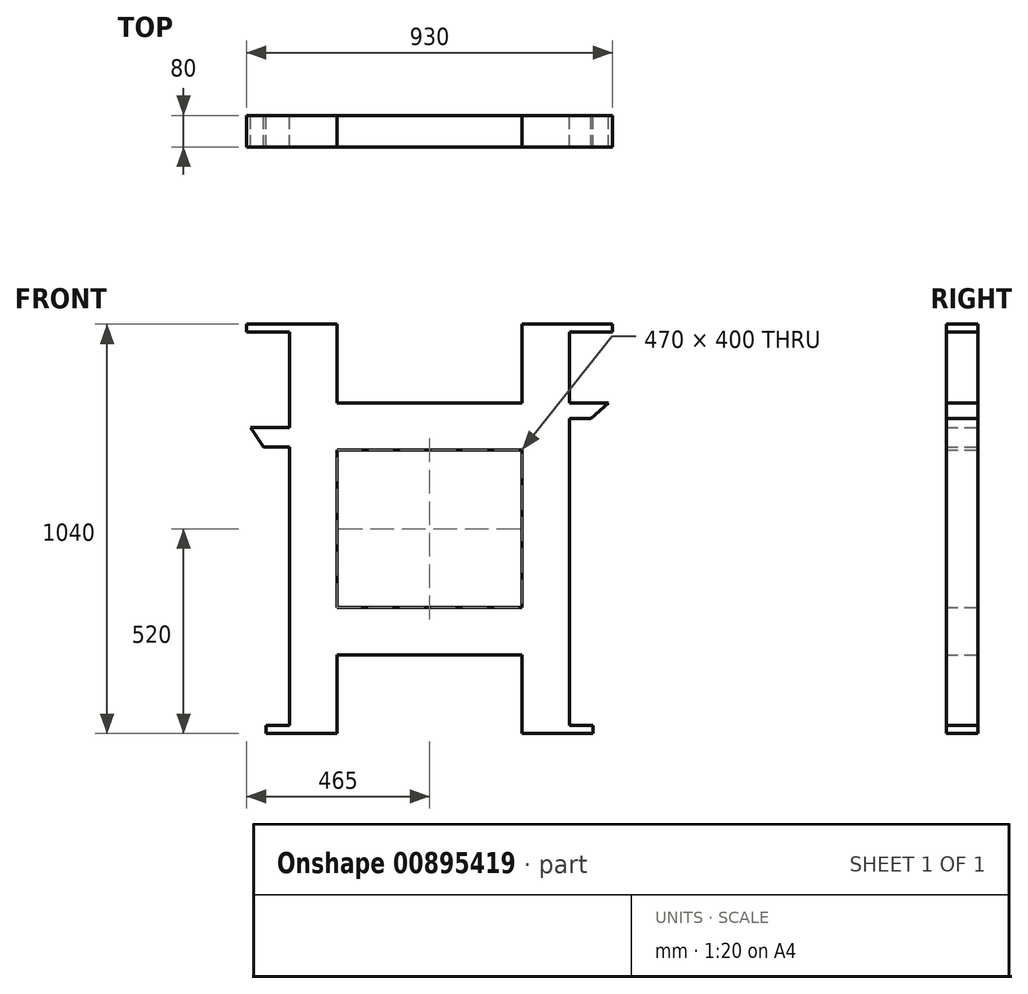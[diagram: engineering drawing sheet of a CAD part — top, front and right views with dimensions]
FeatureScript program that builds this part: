
annotation { "Feature Type Name" : "Feature", "Feature Type Description" : "" }
export const myFeature = defineFeature(function(context is Context, id is Id, definition is map)
    precondition{}
    {
        {
            var Q0;
            Q0=qCreatedBy(makeId("Front.planeOp"),FACE);
            var sketch = newSketch(context, id + "F0", { "sketchPlane" : qUnion([Q0])});
            skLineSegment(sketch, "E0.bottom", {"start": v(-355, 0) * mm, "end": v(-235, 0) * mm});
            skLineSegment(sketch, "E0.top", {"start": v(-355, -1040) * mm, "end": v(-235, -1040) * mm});
            skLineSegment(sketch, "E0.left", {"start": v(-355, -20) * mm, "end": v(-355, -262.18) * mm});
            skLineSegment(sketch, "E0.right", {"start": v(355, -20) * mm, "end": v(355, -200) * mm});
            skLineSegment(sketch, "E1.top", {"start": v(-235, -840) * mm, "end": v(235, -840) * mm});
            skLineSegment(sketch, "E1.left", {"start": v(-235, -1040) * mm, "end": v(-235, -840) * mm});
            skLineSegment(sketch, "E1.right", {"start": v(235, -1040) * mm, "end": v(235, -840) * mm});
            skLineSegment(sketch, "E2.bottom", {"start": v(-235, -720) * mm, "end": v(235, -720) * mm});
            skLineSegment(sketch, "E2.top", {"start": v(-235, -320) * mm, "end": v(235, -320) * mm});
            skLineSegment(sketch, "E2.left", {"start": v(-235, -720) * mm, "end": v(-235, -320) * mm});
            skLineSegment(sketch, "E2.right", {"start": v(235, -720) * mm, "end": v(235, -320) * mm});
            skLineSegment(sketch, "E3.bottom", {"start": v(-235, -200) * mm, "end": v(235, -200) * mm});
            skLineSegment(sketch, "E3.left", {"start": v(-235, -200) * mm, "end": v(-235, 0) * mm});
            skLineSegment(sketch, "E3.right", {"start": v(235, -200) * mm, "end": v(235, 0) * mm});
            skLineSegment(sketch, "E4.bottom", {"start": v(-355, 0) * mm, "end": v(-465, 0) * mm});
            skLineSegment(sketch, "E4.top", {"start": v(-355, -20) * mm, "end": v(-465, -20) * mm});
            skLineSegment(sketch, "E4.right", {"start": v(-465, 0) * mm, "end": v(-465, -20) * mm});
            skLineSegment(sketch, "E5.bottom", {"start": v(355, 0) * mm, "end": v(465, 0) * mm});
            skLineSegment(sketch, "E5.top", {"start": v(355, -20) * mm, "end": v(465, -20) * mm});
            skLineSegment(sketch, "E5.right", {"start": v(465, 0) * mm, "end": v(465, -20) * mm});
            skLineSegment(sketch, "E6.bottom", {"start": v(355, -1040) * mm, "end": v(415, -1040) * mm});
            skLineSegment(sketch, "E6.top", {"start": v(355, -1020) * mm, "end": v(415, -1020) * mm});
            skLineSegment(sketch, "E6.left", {"start": v(355, -1040) * mm, "end": v(355, -1020) * mm});
            skLineSegment(sketch, "E6.right", {"start": v(415, -1040) * mm, "end": v(415, -1020) * mm});
            skLineSegment(sketch, "E7.bottom", {"start": v(-355, -1040) * mm, "end": v(-415, -1040) * mm});
            skLineSegment(sketch, "E7.top", {"start": v(-355, -1020) * mm, "end": v(-415, -1020) * mm});
            skLineSegment(sketch, "E7.left", {"start": v(-355, -1040) * mm, "end": v(-355, -1020) * mm});
            skLineSegment(sketch, "E7.right", {"start": v(-415, -1040) * mm, "end": v(-415, -1020) * mm});
            skLineSegment(sketch, "E8.trimOffspring", {"start": v(235, 0) * mm, "end": v(355, 0) * mm});
            skLineSegment(sketch, "E9.trimOffspring", {"start": v(235, -1040) * mm, "end": v(355, -1040) * mm});
            skLineSegment(sketch, "E10.bottom", {"start": v(-355, -312.18) * mm, "end": v(-421.83, -312.18) * mm});
            skLineSegment(sketch, "E10.top", {"start": v(-355, -262.18) * mm, "end": v(-455, -262.18) * mm});
            skLineSegment(sketch, "E11", {"start": v(-455, -262.18) * mm, "end": v(-421.83, -312.18) * mm});
            skLineSegment(sketch, "E12.bottom", {"start": v(355, -200) * mm, "end": v(455, -200) * mm});
            skLineSegment(sketch, "E12.top", {"start": v(355, -240) * mm, "end": v(410.28, -240) * mm});
            skLineSegment(sketch, "E13", {"start": v(455, -200) * mm, "end": v(410.28, -240) * mm});
            skLineSegment(sketch, "E14.trimOffspring", {"start": v(-355, -312.18) * mm, "end": v(-355, -1040) * mm});
            skLineSegment(sketch, "E15.trimOffspring", {"start": v(355, -240) * mm, "end": v(355, -1040) * mm});
            skSolve(sketch);
        }
        {
            var Q0;
            Q0 = qSketchRegion(id + "F0", true);
            extrude(context, id + "F1", {"entities" : qUnion([Q0]), "depth" : 80 * mm, "offsetDistance" : 25 * mm});
        }
    });
